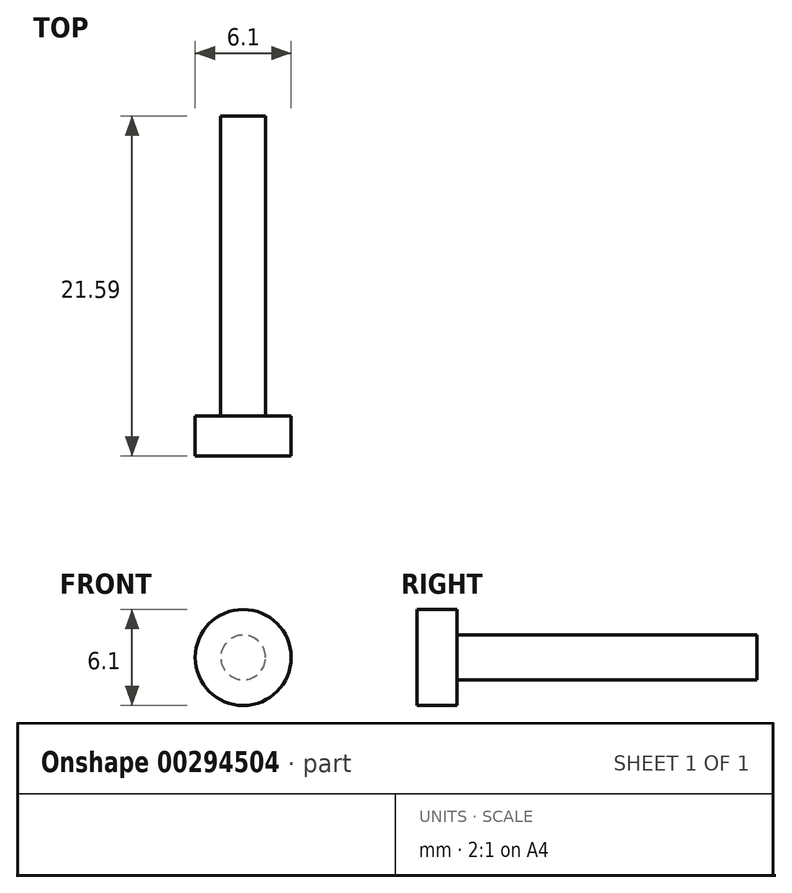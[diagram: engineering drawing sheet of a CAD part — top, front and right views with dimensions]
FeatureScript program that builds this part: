
annotation { "Feature Type Name" : "Feature", "Feature Type Description" : "" }
export const myFeature = defineFeature(function(context is Context, id is Id, definition is map)
    precondition{}
    {
        {
            var Q0;
            Q0=qCreatedBy(makeId("Right.planeOp"),FACE);
            var sketch = newSketch(context, id + "F0", { "sketchPlane" : qUnion([Q0])});
            skLineSegment(sketch, "E0", {"start": v(0, 0) * mm, "end": v(0, 3.05) * mm});
            skLineSegment(sketch, "E1", {"start": v(0, 3.05) * mm, "end": v(2.54, 3.05) * mm});
            skLineSegment(sketch, "E2", {"start": v(2.54, 3.05) * mm, "end": v(2.54, 1.42) * mm});
            skLineSegment(sketch, "E3", {"start": v(2.54, 1.42) * mm, "end": v(21.59, 1.42) * mm});
            skLineSegment(sketch, "E4", {"start": v(21.59, 1.42) * mm, "end": v(21.59, 0) * mm});
            skLineSegment(sketch, "E5", {"start": v(21.59, 0) * mm, "end": v(0, 0) * mm});
            skSolve(sketch);
        }
        {
            var Q0;
            Q0 = qSketchRegion(id + "F0", true);
            var Q1;
            Q1=sQuery(id+"F0.wireOp",EDGE,"E5");
            revolve(context, id + "F1", {"entities" : qUnion([Q0]), "axis" : qUnion([Q1]), "revolveType" : RevolveType.FULL});
        }
    });
